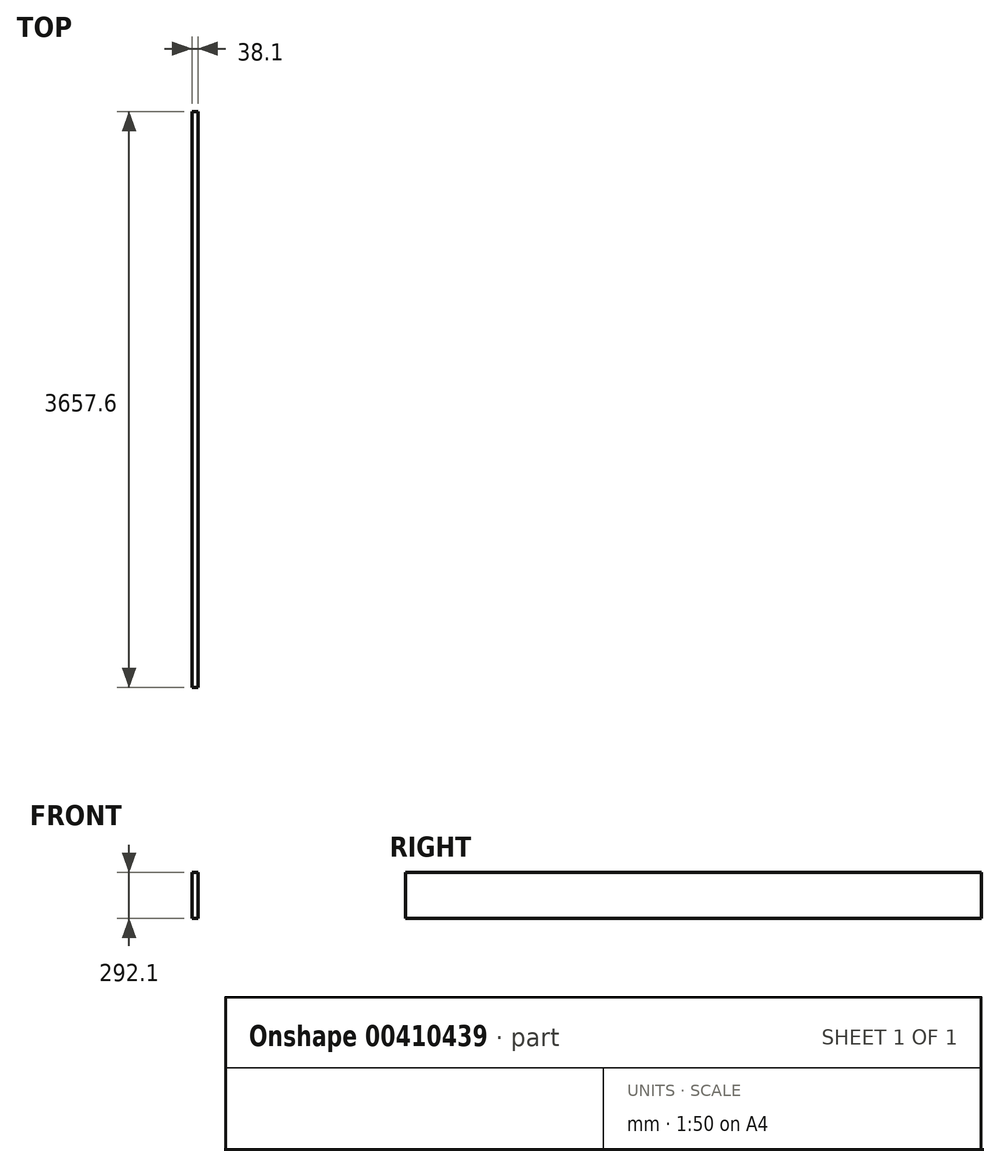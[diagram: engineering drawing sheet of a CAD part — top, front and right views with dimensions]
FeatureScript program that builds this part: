
annotation { "Feature Type Name" : "Feature", "Feature Type Description" : "" }
export const myFeature = defineFeature(function(context is Context, id is Id, definition is map)
    precondition{}
    {
        {
            var Q0;
            Q0=qCreatedBy(makeId("Right.planeOp"),FACE);
            var sketch = newSketch(context, id + "F0", { "sketchPlane" : qUnion([Q0])});
            skLineSegment(sketch, "E0.bottom", {"start": v(-1828.8, 146.05) * mm, "end": v(1828.8, 146.05) * mm});
            skLineSegment(sketch, "E0.top", {"start": v(-1828.8, -146.05) * mm, "end": v(1828.8, -146.05) * mm});
            skLineSegment(sketch, "E0.left", {"start": v(-1828.8, 146.05) * mm, "end": v(-1828.8, -146.05) * mm});
            skLineSegment(sketch, "E0.right", {"start": v(1828.8, 146.05) * mm, "end": v(1828.8, -146.05) * mm});
            skPoint(sketch, "E0.middle", {"position": v(0, 0) * mm});
            skSolve(sketch);
        }
        {
            var Q0;
            Q0=qSketchRegion(id+"F0",true);
            extrude(context, id + "F1", {"entities" : qUnion([Q0]), "depth" : 38.1 * mm, "offsetDistance" : 25.4 * mm});
        }
    });
